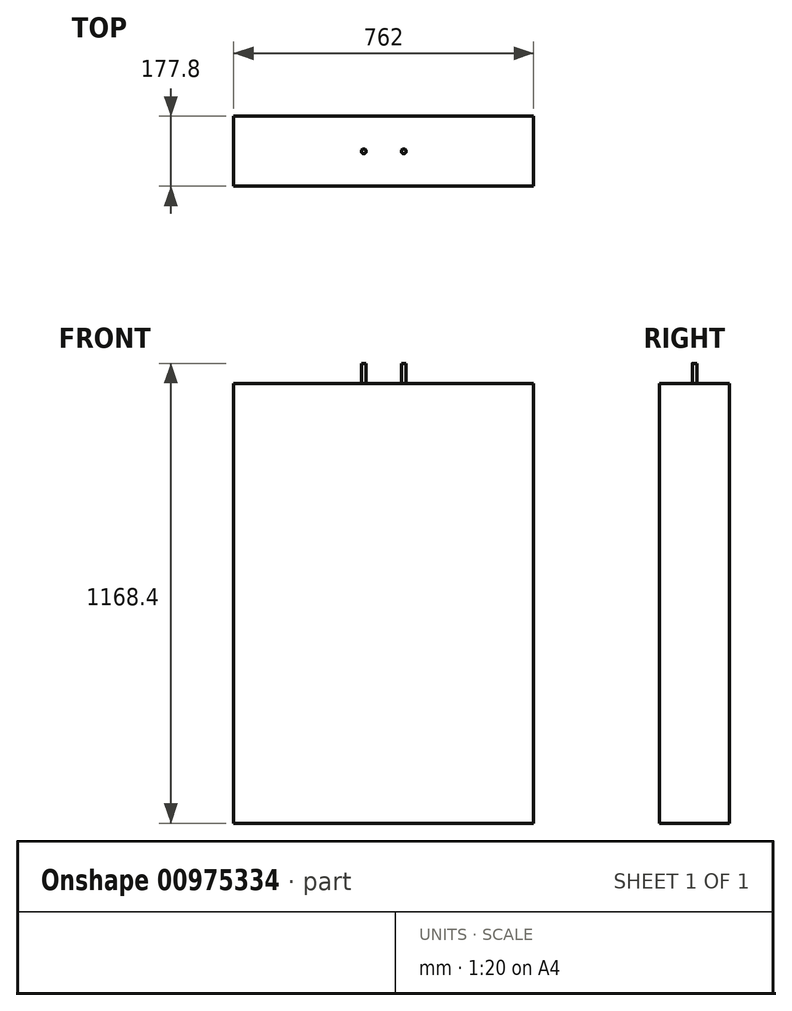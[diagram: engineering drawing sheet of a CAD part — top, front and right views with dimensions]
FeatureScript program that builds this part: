
annotation { "Feature Type Name" : "Feature", "Feature Type Description" : "" }
export const myFeature = defineFeature(function(context is Context, id is Id, definition is map)
    precondition{}
    {
        {
            var Q0;
            Q0=qCreatedBy(makeId("Front.planeOp"),FACE);
            var sketch = newSketch(context, id + "F0", { "sketchPlane" : qUnion([Q0])});
            skLineSegment(sketch, "E0.bottom", {"start": v(-453.58, 664.65) * mm, "end": v(308.42, 664.65) * mm});
            skLineSegment(sketch, "E0.top", {"start": v(-453.58, -452.95) * mm, "end": v(308.42, -452.95) * mm});
            skLineSegment(sketch, "E0.left", {"start": v(-453.58, 664.65) * mm, "end": v(-453.58, -452.95) * mm});
            skLineSegment(sketch, "E0.right", {"start": v(308.42, 664.65) * mm, "end": v(308.42, -452.95) * mm});
            skSolve(sketch);
        }
        {
            var Q0;
            Q0=makeQuery(id+"F0.imprint","IMPRINT",FACE,{"disambiguationData":[TD([[makeQuery(id+"F0.imprint","IMPRINT",EDGE,{"derivedFrom":sQuery(id+"F0.wireOp",EDGE,"E0.bottom")}),-1.0]])]});
            extrude(context, id + "F1", {"entities" : qUnion([Q0]), "depth" : 177.8 * mm, "offsetDistance" : 25.4 * mm});
        }
        {
            var Q0;
            Q0=makeQuery(id+"F1.opExtrude","SWEPT_FACE",FACE,{"disambiguationData":[OSD([sQuery(id+"F0.wireOp",EDGE,"E0.bottom")])]});
            var sketch = newSketch(context, id + "F2", { "sketchPlane" : qUnion([Q0])});
            skPoint(sketch, "E1", {"position": v(-72.58, 0) * mm});
            skPoint(sketch, "E2", {"position": v(-453.58, -88.9) * mm});
            skLineSegment(sketch, "E3", {"start": v(-453.58, -88.9) * mm, "end": v(-72.58, -88.9) * mm, "construction": true});
            skLineSegment(sketch, "E4", {"start": v(-72.58, 0) * mm, "end": v(-72.58, -88.9) * mm, "construction": true});
            skPoint(sketch, "E5", {"position": v(-21.78, -88.9) * mm});
            skPoint(sketch, "E6", {"position": v(-123.38, -88.9) * mm});
            skCircle(sketch, "E7", {"center": v(-123.38, -88.9) * mm, "radius": 6.1 * mm});
            skCircle(sketch, "E8", {"center": v(-21.78, -88.9) * mm, "radius": 6.1 * mm});
            skSolve(sketch);
        }
        {
            var Q0;
            Q0 = qSketchRegion(id + "F2", true);
            extrude(context, id + "F3", {"entities" : qUnion([Q0]), "operationType" : NewBodyOperationType.ADD, "depth" : 50.8 * mm, "offsetDistance" : 25.4 * mm});
        }
    });
